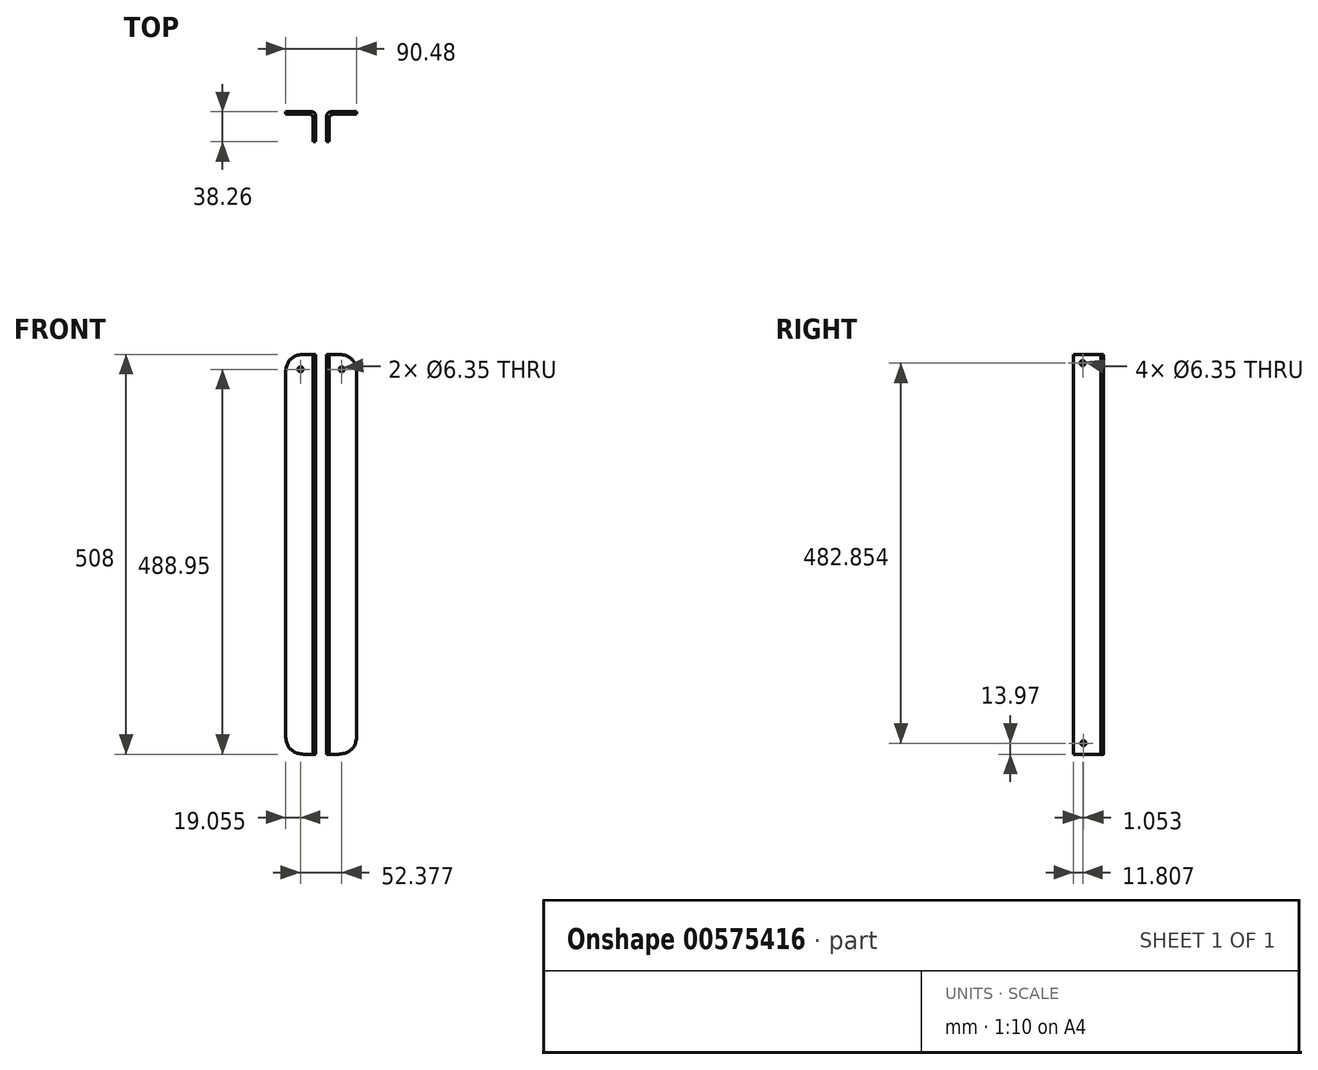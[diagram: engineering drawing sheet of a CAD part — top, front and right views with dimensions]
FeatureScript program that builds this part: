
annotation { "Feature Type Name" : "Feature", "Feature Type Description" : "" }
export const myFeature = defineFeature(function(context is Context, id is Id, definition is map)
    precondition{}
    {
        {
            var Q0;
            Q0=qCreatedBy(makeId("Top.planeOp"),FACE);
            var sketch = newSketch(context, id + "F0", { "sketchPlane" : qUnion([Q0])});
            skLineSegment(sketch, "E0", {"start": v(-34.92, 20.97) * mm, "end": v(0, 20.97) * mm});
            skLineSegment(sketch, "E1", {"start": v(0, 20.97) * mm, "end": v(0, -13.95) * mm});
            skLineSegment(sketch, "E2", {"start": v(0, -13.95) * mm, "end": v(3.18, -13.95) * mm});
            skLineSegment(sketch, "E3", {"start": v(3.18, -13.95) * mm, "end": v(3.18, 24.15) * mm});
            skLineSegment(sketch, "E4", {"start": v(3.18, 24.15) * mm, "end": v(-34.92, 24.15) * mm});
            skLineSegment(sketch, "E5", {"start": v(-34.92, 24.15) * mm, "end": v(-34.92, 20.97) * mm});
            skSolve(sketch);
        }
        {
            var Q0;
            Q0=makeQuery(id+"F0.imprint","IMPRINT",FACE,{"disambiguationData":[TD([[makeQuery(id+"F0.imprint","IMPRINT",EDGE,{"derivedFrom":sQuery(id+"F0.wireOp",EDGE,"E0")}),1.0]])]});
            extrude(context, id + "F1", {"entities" : qUnion([Q0]), "depth" : 508 * mm, "offsetDistance" : 25.4 * mm});
        }
        {
            var Q0;
            Q0=makeQuery(id+"F1.opExtrude","SWEPT_FACE",FACE,{"disambiguationData":[OSD([sQuery(id+"F0.wireOp",EDGE,"E1")])]});
            var sketch = newSketch(context, id + "F2", { "sketchPlane" : qUnion([Q0])});
            skCircle(sketch, "E6", {"center": v(2.14, 496.82) * mm, "radius": 3.18 * mm});
            skSolve(sketch);
        }
        {
            var Q0;
            Q0=makeQuery(id+"F2.imprint","IMPRINT",FACE,{"disambiguationData":[TD([[makeQuery(id+"F2.imprint","IMPRINT",EDGE,{"derivedFrom":sQuery(id+"F2.wireOp",EDGE,"E6")}),1.0]])]});
            extrude(context, id + "F3", {"entities" : qUnion([Q0]), "operationType" : NewBodyOperationType.REMOVE, "oppositeDirection" : true, "depth" : 3.17 * mm, "offsetDistance" : 25.4 * mm});
        }
        {
            var Q0;
            Q0=makeQuery(id+"F1.opExtrude","SWEPT_FACE",FACE,{"disambiguationData":[OSD([sQuery(id+"F0.wireOp",EDGE,"E1")])]});
            var sketch = newSketch(context, id + "F4", { "sketchPlane" : qUnion([Q0])});
            skCircle(sketch, "E7", {"center": v(1.25, 13.97) * mm, "radius": 3.18 * mm});
            skSolve(sketch);
        }
        {
            var Q0;
            Q0=makeQuery(id+"F4.imprint","IMPRINT",FACE,{"disambiguationData":[TD([[makeQuery(id+"F4.imprint","IMPRINT",EDGE,{"derivedFrom":sQuery(id+"F4.wireOp",EDGE,"E7")}),1.0]])]});
            extrude(context, id + "F5", {"entities" : qUnion([Q0]), "operationType" : NewBodyOperationType.REMOVE, "oppositeDirection" : true, "depth" : 3.17 * mm, "offsetDistance" : 25.4 * mm});
        }
        {
            var Q0;
            Q0=qCreatedBy(makeId("Top.planeOp"),FACE);
            var sketch = newSketch(context, id + "F6", { "sketchPlane" : qUnion([Q0])});
            skLineSegment(sketch, "E8", {"start": v(17.45, -14.11) * mm, "end": v(17.45, 23.99) * mm});
            skLineSegment(sketch, "E9", {"start": v(17.45, 23.99) * mm, "end": v(55.55, 23.99) * mm});
            skLineSegment(sketch, "E10", {"start": v(55.55, 23.99) * mm, "end": v(55.55, 20.81) * mm});
            skLineSegment(sketch, "E11", {"start": v(55.55, 20.81) * mm, "end": v(20.63, 20.81) * mm});
            skLineSegment(sketch, "E12", {"start": v(20.63, 20.81) * mm, "end": v(20.63, -14.11) * mm});
            skLineSegment(sketch, "E13", {"start": v(20.63, -14.11) * mm, "end": v(17.45, -14.11) * mm});
            skSolve(sketch);
        }
        {
            var Q0;
            Q0=makeQuery(id+"F6.imprint","IMPRINT",FACE,{"disambiguationData":[TD([[makeQuery(id+"F6.imprint","IMPRINT",EDGE,{"derivedFrom":sQuery(id+"F6.wireOp",EDGE,"E8")}),-1.0]])]});
            extrude(context, id + "F7", {"entities" : qUnion([Q0]), "depth" : 508 * mm, "offsetDistance" : 25.4 * mm});
        }
        {
            var Q0;
            Q0=makeQuery(id+"F7.opExtrude","SWEPT_FACE",FACE,{"disambiguationData":[OSD([sQuery(id+"F6.wireOp",EDGE,"E8")])]});
            var sketch = newSketch(context, id + "F8", { "sketchPlane" : qUnion([Q0])});
            skCircle(sketch, "E14", {"center": v(2.3, 496.82) * mm, "radius": 3.18 * mm});
            skSolve(sketch);
        }
        {
            var Q0;
            Q0=makeQuery(id+"F8.imprint","IMPRINT",FACE,{"disambiguationData":[TD([[makeQuery(id+"F8.imprint","IMPRINT",EDGE,{"derivedFrom":sQuery(id+"F8.wireOp",EDGE,"E14")}),1.0]])]});
            extrude(context, id + "F9", {"entities" : qUnion([Q0]), "operationType" : NewBodyOperationType.REMOVE, "oppositeDirection" : true, "depth" : 3.17 * mm, "offsetDistance" : 25.4 * mm});
        }
        {
            var Q0;
            Q0=makeQuery(id+"F7.opExtrude","SWEPT_FACE",FACE,{"disambiguationData":[OSD([sQuery(id+"F6.wireOp",EDGE,"E8")])]});
            var sketch = newSketch(context, id + "F10", { "sketchPlane" : qUnion([Q0])});
            skCircle(sketch, "E15", {"center": v(1.41, 13.97) * mm, "radius": 3.18 * mm});
            skSolve(sketch);
        }
        {
            var Q0;
            Q0 = qSketchRegion(id + "F10", true);
            extrude(context, id + "F11", {"entities" : qUnion([Q0]), "operationType" : NewBodyOperationType.REMOVE, "oppositeDirection" : true, "depth" : 3.17 * mm, "offsetDistance" : 25.4 * mm});
        }
        {
            var Q0;
            Q0=makeQuery(id+"F7.opExtrude","SWEPT_FACE",FACE,{"disambiguationData":[OSD([sQuery(id+"F6.wireOp",EDGE,"E9")])]});
            var sketch = newSketch(context, id + "F12", { "sketchPlane" : qUnion([Q0])});
            skCircle(sketch, "E16", {"center": v(-36.5, 488.95) * mm, "radius": 3.18 * mm});
            skSolve(sketch);
        }
        {
            var Q0;
            Q0=makeQuery(id+"F12.imprint","IMPRINT",FACE,{"disambiguationData":[TD([[makeQuery(id+"F12.imprint","IMPRINT",EDGE,{"derivedFrom":sQuery(id+"F12.wireOp",EDGE,"E16")}),1.0]])]});
            extrude(context, id + "F13", {"entities" : qUnion([Q0]), "operationType" : NewBodyOperationType.REMOVE, "oppositeDirection" : true, "depth" : 3.17 * mm, "offsetDistance" : 25.4 * mm});
        }
        {
            var Q0;
            Q0=makeQuery(id+"F7.opExtrude","CAP_EDGE",EDGE,{"disambiguationData":[OSD([sQuery(id+"F6.wireOp",EDGE,"E10")])],"isStart":false});
            fillet(context, id + "F14", {"entities" : qUnion([Q0]), "radius" : 25.4 * mm, "tangentPropagation" : true, "rho" : 0.5, "crossSection" : FilletCrossSection.CONIC, "allowEdgeOverflow" : false});
        }
        {
            var Q0;
            Q0=makeQuery(id+"F1.opExtrude","SWEPT_FACE",FACE,{"disambiguationData":[OSD([sQuery(id+"F0.wireOp",EDGE,"E4")])]});
            var sketch = newSketch(context, id + "F15", { "sketchPlane" : qUnion([Q0])});
            skCircle(sketch, "E17", {"center": v(15.87, 488.95) * mm, "radius": 3.18 * mm});
            skSolve(sketch);
        }
        {
            var Q0;
            Q0=makeQuery(id+"F1.opExtrude","CAP_EDGE",EDGE,{"disambiguationData":[OSD([sQuery(id+"F0.wireOp",EDGE,"E5")])],"isStart":false});
            fillet(context, id + "F16", {"entities" : qUnion([Q0]), "radius" : 25.4 * mm, "tangentPropagation" : true, "rho" : 0.5, "crossSection" : FilletCrossSection.CONIC, "allowEdgeOverflow" : false});
        }
        {
            var Q0;
            Q0=makeQuery(id+"F15.imprint","IMPRINT",FACE,{"disambiguationData":[TD([[makeQuery(id+"F15.imprint","IMPRINT",EDGE,{"derivedFrom":sQuery(id+"F15.wireOp",EDGE,"E17")}),1.0]])]});
            extrude(context, id + "F17", {"entities" : qUnion([Q0]), "operationType" : NewBodyOperationType.REMOVE, "oppositeDirection" : true, "depth" : 3.17 * mm, "offsetDistance" : 25.4 * mm});
        }
        {
            var Q0;
            Q0=makeQuery(id+"F7.opExtrude","CAP_EDGE",EDGE,{"disambiguationData":[OSD([sQuery(id+"F6.wireOp",EDGE,"E10")])],"isStart":true});
            var Q1;
            Q1=makeQuery(id+"F1.opExtrude","CAP_EDGE",EDGE,{"disambiguationData":[OSD([sQuery(id+"F0.wireOp",EDGE,"E5")])],"isStart":true});
            fillet(context, id + "F18", {"entities" : qUnion([Q0, Q1]), "radius" : 25.4 * mm, "tangentPropagation" : true, "rho" : 0.5, "crossSection" : FilletCrossSection.CONIC, "allowEdgeOverflow" : false});
        }
        {
            var Q0;
            Q0=makeQuery(id+"F7.opExtrude","SWEPT_EDGE",EDGE,{"disambiguationData":[OSD([sQuery(id+"F6.wireOp",EDGE,"E11"),sQuery(id+"F6.wireOp",EDGE,"E12")])]});
            var Q1;
            Q1=makeQuery(id+"F1.opExtrude","SWEPT_EDGE",EDGE,{"disambiguationData":[OSD([sQuery(id+"F0.wireOp",EDGE,"E0"),sQuery(id+"F0.wireOp",EDGE,"E1")])]});
            var Q2;
            Q2=makeQuery(id+"F7.opExtrude","SWEPT_EDGE",EDGE,{"disambiguationData":[OSD([sQuery(id+"F6.wireOp",EDGE,"E8"),sQuery(id+"F6.wireOp",EDGE,"E9")])]});
            var Q3;
            Q3=makeQuery(id+"F1.opExtrude","SWEPT_EDGE",EDGE,{"disambiguationData":[OSD([sQuery(id+"F0.wireOp",EDGE,"E3"),sQuery(id+"F0.wireOp",EDGE,"E4")])]});
            fillet(context, id + "F19", {"entities" : qUnion([Q0, Q1, Q2, Q3]), "radius" : 5.08 * mm, "tangentPropagation" : true, "allowEdgeOverflow" : false});
        }
    });
